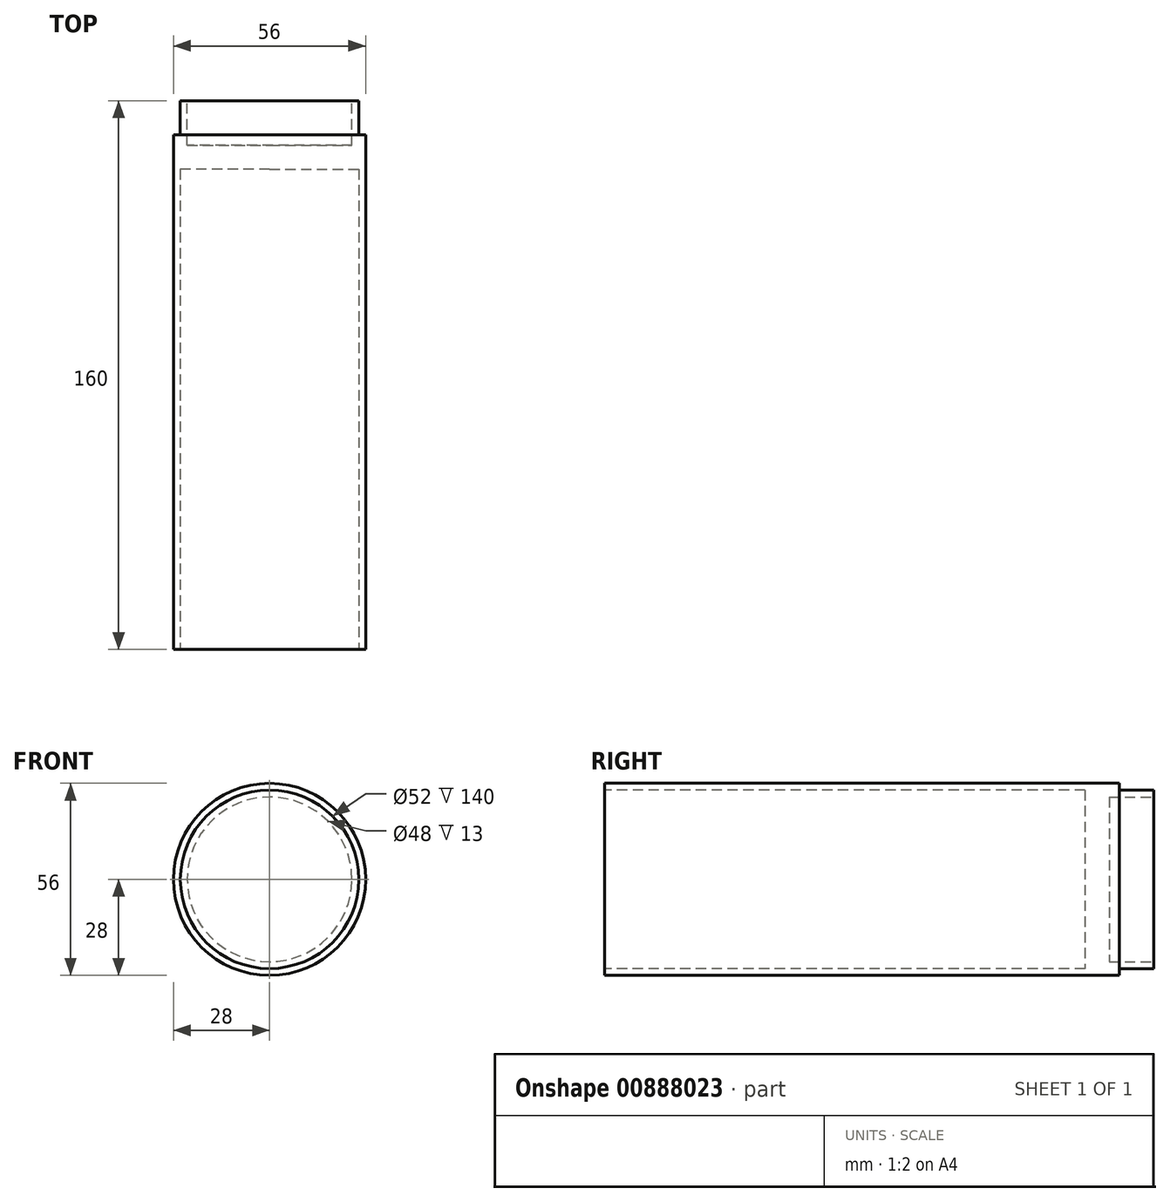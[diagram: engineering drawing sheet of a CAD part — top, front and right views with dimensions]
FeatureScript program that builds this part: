
annotation { "Feature Type Name" : "Feature", "Feature Type Description" : "" }
export const myFeature = defineFeature(function(context is Context, id is Id, definition is map)
    precondition{}
    {
        {
            var Q0;
            Q0=qCreatedBy(makeId("Right.planeOp"),FACE);
            var sketch = newSketch(context, id + "F0", { "sketchPlane" : qUnion([Q0])});
            skLineSegment(sketch, "E0", {"start": v(-7.5, 0) * mm, "end": v(59.13, 0) * mm});
            skLineSegment(sketch, "E1.bottom", {"start": v(-75, -26) * mm, "end": v(75, -26) * mm});
            skLineSegment(sketch, "E1.top", {"start": v(-75, -28) * mm, "end": v(75, -28) * mm});
            skLineSegment(sketch, "E1.left", {"start": v(-75, -26) * mm, "end": v(-75, -28) * mm});
            skLineSegment(sketch, "E1.right", {"start": v(75, -26) * mm, "end": v(75, -28) * mm});
            skPoint(sketch, "E1.middle", {"position": v(0, -27) * mm});
            skSolve(sketch);
        }
        {
            var Q0;
            Q0=makeQuery(id+"F0.imprint","IMPRINT",FACE,{"disambiguationData":[TD([[makeQuery(id+"F0.imprint","IMPRINT",EDGE,{"derivedFrom":sQuery(id+"F0.wireOp",EDGE,"E1.bottom")}),-1.0]])]});
            var Q1;
            Q1=sQuery(id+"F0.wireOp",EDGE,"E0");
            revolve(context, id + "F1", {"entities" : qUnion([Q0]), "axis" : qUnion([Q1]), "revolveType" : RevolveType.FULL});
        }
        {
            var Q0;
            Q0=makeQuery(id+"F1.opRevolve","SWEPT_FACE",FACE,{"disambiguationData":[OSD([sQuery(id+"F0.wireOp",EDGE,"E1.right")])]});
            var sketch = newSketch(context, id + "F2", { "sketchPlane" : qUnion([Q0])});
            skCircle(sketch, "E2", {"center": v(0, 0) * mm, "radius": 26 * mm});
            skSolve(sketch);
        }
        {
            var Q0;
            Q0=qSketchRegion(id+"F2",true);
            extrude(context, id + "F3", {"entities" : qUnion([Q0]), "operationType" : NewBodyOperationType.ADD, "endBound" : BoundingType.SYMMETRIC, "depth" : 20 * mm, "offsetDistance" : 25 * mm});
        }
        {
            var Q0;
            Q0=makeQuery(id+"F3.opExtrude","CAP_FACE",FACE,{"disambiguationData":[OSD([sQuery(id+"F2.wireOp",EDGE,"E2")])],"isStart":false});
            var sketch = newSketch(context, id + "F4", { "sketchPlane" : qUnion([Q0])});
            skCircle(sketch, "E3", {"center": v(0, 0) * mm, "radius": 24 * mm});
            skSolve(sketch);
        }
        {
            var Q0;
            Q0=qSketchRegion(id+"F4",true);
            extrude(context, id + "F5", {"entities" : qUnion([Q0]), "operationType" : NewBodyOperationType.REMOVE, "oppositeDirection" : true, "depth" : 13 * mm, "offsetDistance" : 25 * mm});
        }
    });
